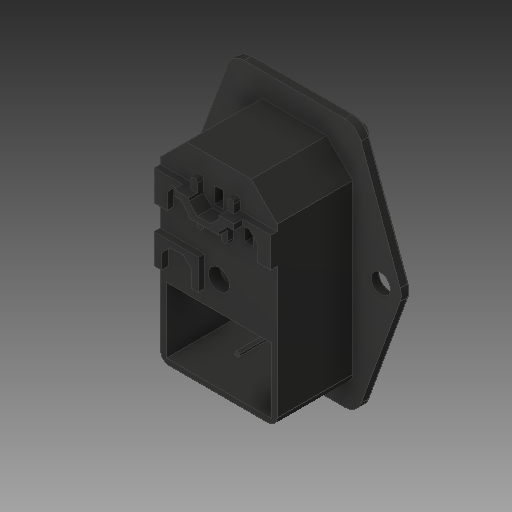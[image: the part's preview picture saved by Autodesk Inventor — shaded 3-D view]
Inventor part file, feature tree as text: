
AUTODESK INVENTOR PART (.ipt)
format: ipt  version: 2019.4 (Build 234330000, 330)  size: 281,600 bytes
history: native  units: mm
features: fillet x1
ambient origin geometry x8: Origin, YZ Plane, XZ Plane, XY Plane, X Axis, Y Axis, Z Axis, Center Point
bodies: Solid1 (feature_tree)
feature tree (1):
  fillet  "Fillet1"  [1 undecoded]
note: 1 required parameter value undecoded (feature->parameter linkage not recoverable at this tier; creation-order binding heuristic only, values carry confidence <= 0.55)
